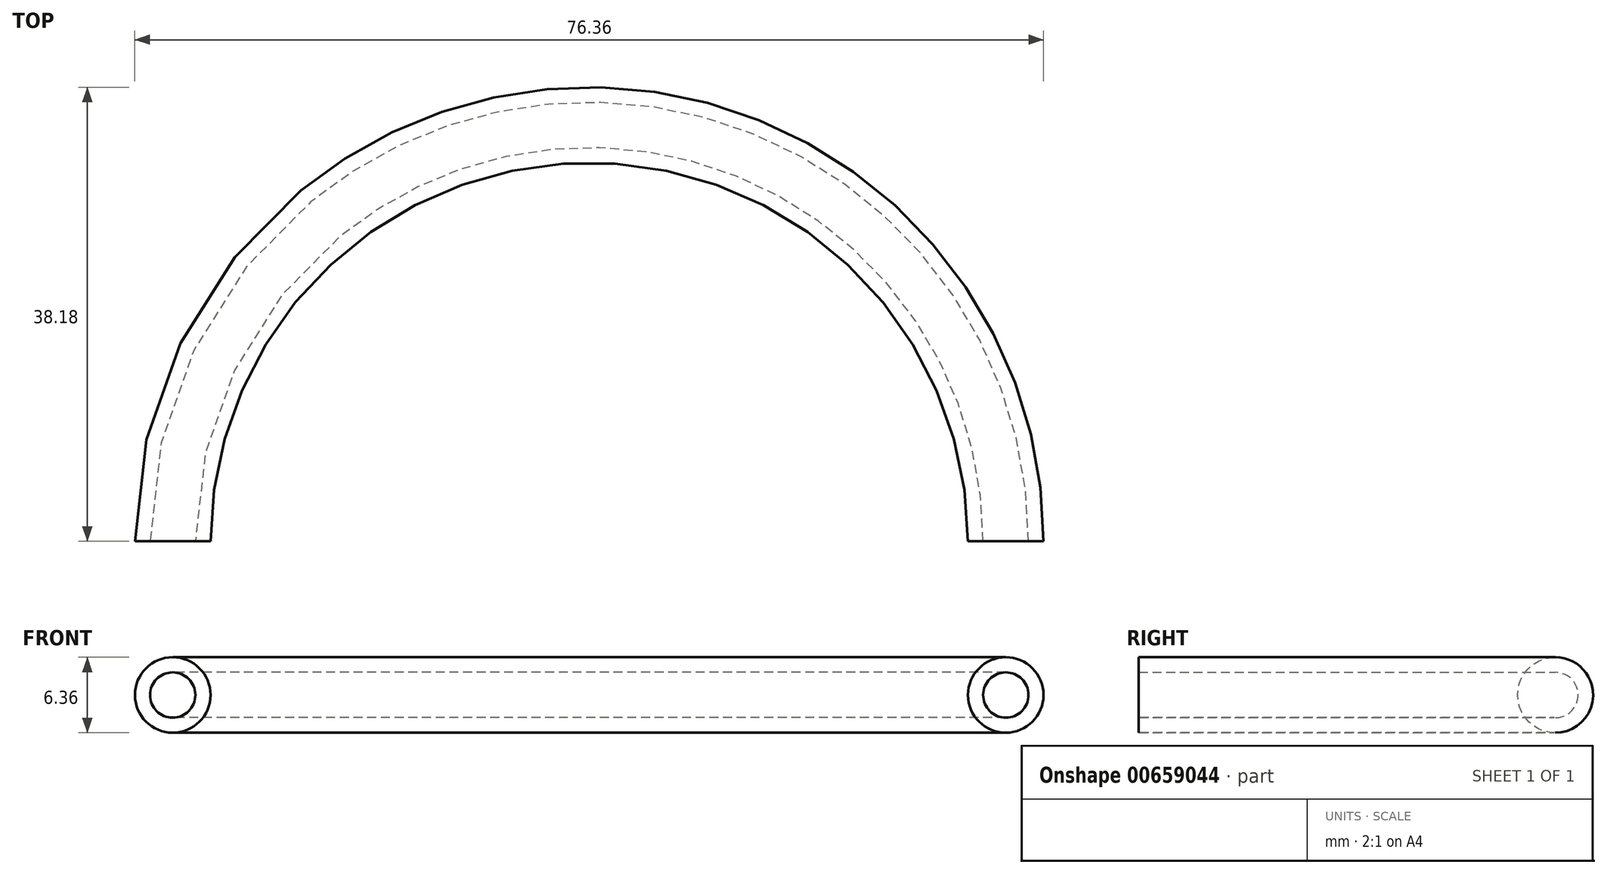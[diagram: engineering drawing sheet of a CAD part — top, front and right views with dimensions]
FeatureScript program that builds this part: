
annotation { "Feature Type Name" : "Feature", "Feature Type Description" : "" }
export const myFeature = defineFeature(function(context is Context, id is Id, definition is map)
    precondition{}
    {
        {
            var Q0;
            Q0=qCreatedBy(makeId("Front.planeOp"),FACE);
            var sketch = newSketch(context, id + "F0", { "sketchPlane" : qUnion([Q0])});
            skCircle(sketch, "E0", {"center": v(0, 0) * mm, "radius": 1.9 * mm});
            skCircle(sketch, "E1", {"center": v(0, 0) * mm, "radius": 3.18 * mm});
            skSolve(sketch);
        }
        {
            var Q0;
            Q0=qCreatedBy(makeId("Front.planeOp"),FACE);
            var sketch = newSketch(context, id + "F1", { "sketchPlane" : qUnion([Q0])});
            skLineSegment(sketch, "E2", {"start": v(35, 23.69) * mm, "end": v(35, -26) * mm});
            skSolve(sketch);
        }
        {
            var Q0;
            Q0=makeQuery(id+"F0.imprint","IMPRINT",FACE,{"disambiguationData":[TD([[makeQuery(id+"F0.imprint","IMPRINT",EDGE,{"derivedFrom":sQuery(id+"F0.wireOp",EDGE,"E0")}),-1.0]])]});
            var Q1;
            Q1=sQuery(id+"F1.wireOp",EDGE,"E2");
            revolve(context, id + "F2", {"entities" : qUnion([Q0]), "axis" : qUnion([Q1]), "revolveType" : RevolveType.ONE_DIRECTION, "angle" : 180 * degree});
        }
    });
